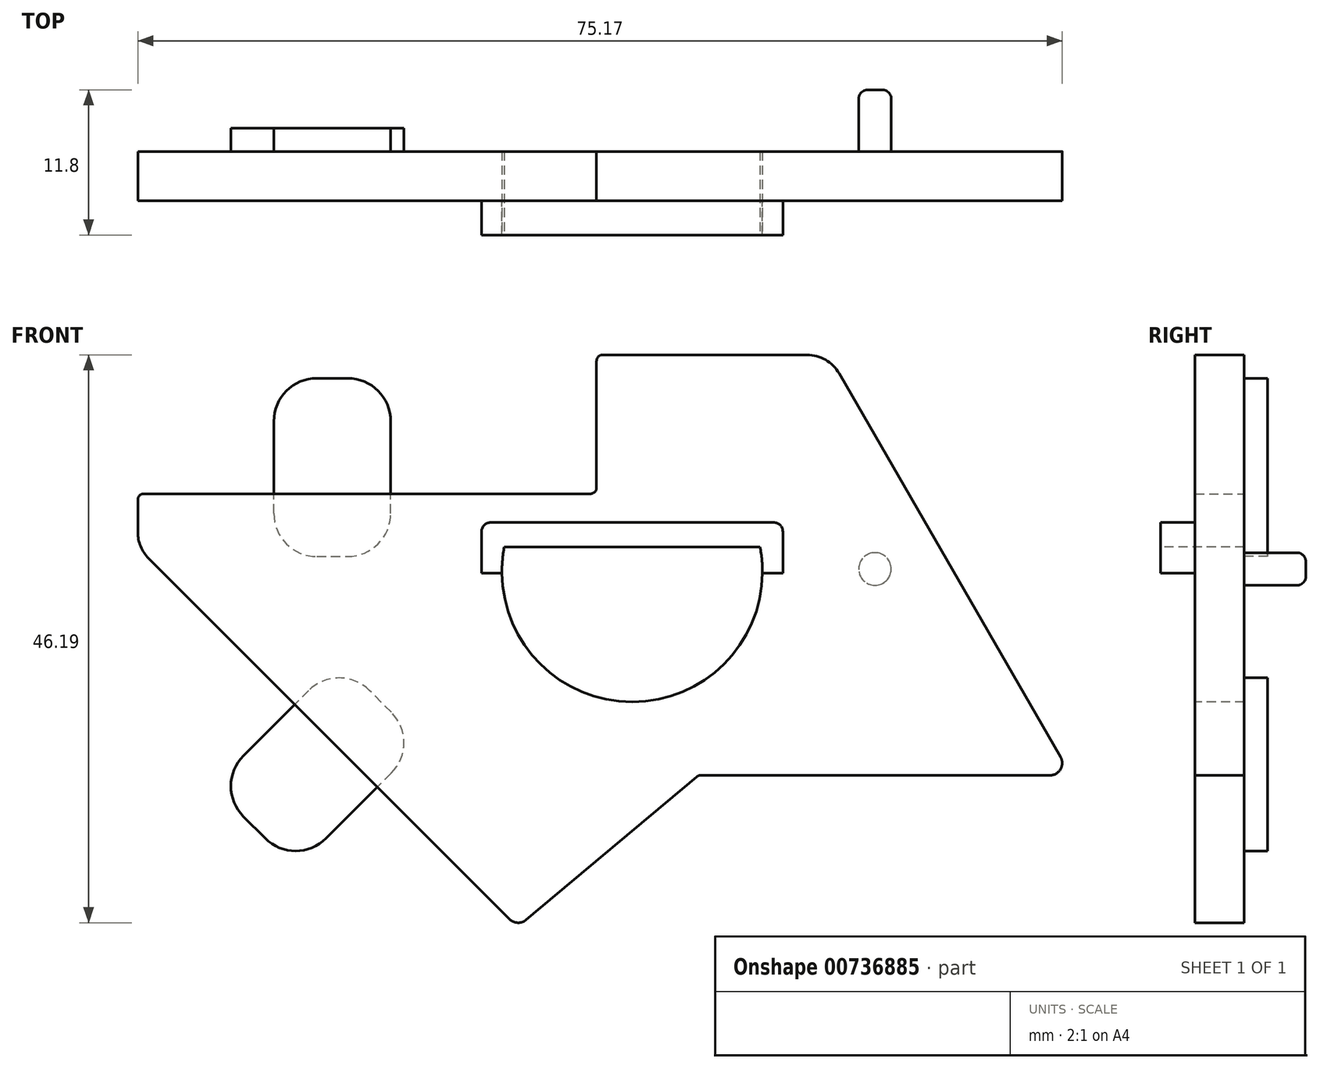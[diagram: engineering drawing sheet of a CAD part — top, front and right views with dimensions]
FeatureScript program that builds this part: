
annotation { "Feature Type Name" : "Feature", "Feature Type Description" : "" }
export const myFeature = defineFeature(function(context is Context, id is Id, definition is map)
    precondition{}
    {
        {
            var Q0;
            Q0=qCreatedBy(makeId("Front.planeOp"),FACE);
            var sketch = newSketch(context, id + "F0", { "sketchPlane" : qUnion([Q0])});
            skLineSegment(sketch, "E0", {"start": v(0, 0) * mm, "end": v(0, 11.3) * mm});
            skLineSegment(sketch, "E1", {"start": v(0, 11.3) * mm, "end": v(18.85, 11.3) * mm});
            skLineSegment(sketch, "E2", {"start": v(18.85, 11.3) * mm, "end": v(38.6, -22.9) * mm});
            skLineSegment(sketch, "E3", {"start": v(38.6, -22.9) * mm, "end": v(8.3, -22.9) * mm});
            skLineSegment(sketch, "E4", {"start": v(8.3, -22.9) * mm, "end": v(-6.42, -35.25) * mm});
            skLineSegment(sketch, "E5", {"start": v(-37.3, 0) * mm, "end": v(0, 0) * mm});
            skLineSegment(sketch, "E6", {"start": v(-37.3, 0) * mm, "end": v(-37.3, -4.37) * mm});
            skLineSegment(sketch, "E7", {"start": v(-37.3, -4.37) * mm, "end": v(-6.42, -35.25) * mm});
            skSolve(sketch);
        }
        {
            var Q0;
            Q0=makeQuery(id+"F0.imprint","IMPRINT",FACE,{"disambiguationData":[TD([[makeQuery(id+"F0.imprint","IMPRINT",EDGE,{"derivedFrom":sQuery(id+"F0.wireOp",EDGE,"E0")}),-1.0]])]});
            extrude(context, id + "F1", {"entities" : qUnion([Q0]), "depth" : 4 * mm, "offsetDistance" : 25 * mm});
        }
        {
            var Q0;
            Q0=makeQuery(id+"F1.opExtrude","SWEPT_EDGE",EDGE,{"disambiguationData":[OSD([sQuery(id+"F0.wireOp",EDGE,"E6"),sQuery(id+"F0.wireOp",EDGE,"E7")])]});
            var Q1;
            Q1=makeQuery(id+"F1.opExtrude","SWEPT_EDGE",EDGE,{"disambiguationData":[OSD([sQuery(id+"F0.wireOp",EDGE,"E1"),sQuery(id+"F0.wireOp",EDGE,"E2")])]});
            fillet(context, id + "F2", {"entities" : qUnion([Q0, Q1]), "radius" : 3 * mm, "tangentPropagation" : true, "allowEdgeOverflow" : false});
        }
        {
            var Q0;
            Q0=makeQuery(id+"F1.opExtrude","SWEPT_EDGE",EDGE,{"disambiguationData":[OSD([sQuery(id+"F0.wireOp",EDGE,"E2"),sQuery(id+"F0.wireOp",EDGE,"E3")])]});
            var Q1;
            Q1=makeQuery(id+"F1.opExtrude","SWEPT_EDGE",EDGE,{"disambiguationData":[OSD([sQuery(id+"F0.wireOp",EDGE,"E4"),sQuery(id+"F0.wireOp",EDGE,"E7")])]});
            fillet(context, id + "F3", {"entities" : qUnion([Q0, Q1]), "radius" : 1 * mm, "tangentPropagation" : true, "allowEdgeOverflow" : false});
        }
        {
            var Q0;
            Q0=makeQuery(id+"F1.opExtrude","SWEPT_EDGE",EDGE,{"disambiguationData":[OSD([sQuery(id+"F0.wireOp",EDGE,"E3"),sQuery(id+"F0.wireOp",EDGE,"E4")])]});
            var Q1;
            Q1=makeQuery(id+"F1.opExtrude","SWEPT_EDGE",EDGE,{"disambiguationData":[OSD([sQuery(id+"F0.wireOp",EDGE,"E0"),sQuery(id+"F0.wireOp",EDGE,"E5")])]});
            var Q2;
            Q2=makeQuery(id+"F1.opExtrude","SWEPT_EDGE",EDGE,{"disambiguationData":[OSD([sQuery(id+"F0.wireOp",EDGE,"E0"),sQuery(id+"F0.wireOp",EDGE,"E1")])]});
            var Q3;
            Q3=makeQuery(id+"F1.opExtrude","SWEPT_EDGE",EDGE,{"disambiguationData":[OSD([sQuery(id+"F0.wireOp",EDGE,"E5"),sQuery(id+"F0.wireOp",EDGE,"E6")])]});
            fillet(context, id + "F4", {"entities" : qUnion([Q0, Q1, Q2, Q3]), "radius" : .5 * mm, "tangentPropagation" : true, "allowEdgeOverflow" : false});
        }
        {
            var Q0;
            Q0=makeQuery(id+"F1.opExtrude","CAP_FACE",FACE,{"disambiguationData":[OSD([sQuery(id+"F0.wireOp",EDGE,"E0"),sQuery(id+"F0.wireOp",EDGE,"E1"),sQuery(id+"F0.wireOp",EDGE,"E2"),sQuery(id+"F0.wireOp",EDGE,"E3"),sQuery(id+"F0.wireOp",EDGE,"E4"),sQuery(id+"F0.wireOp",EDGE,"E5"),sQuery(id+"F0.wireOp",EDGE,"E6"),sQuery(id+"F0.wireOp",EDGE,"E7")])],"isStart":false});
            var sketch = newSketch(context, id + "F5", { "sketchPlane" : qUnion([Q0])});
            skLineSegment(sketch, "E8", {"start": v(-7.5, -4.33) * mm, "end": v(13.3, -4.33) * mm});
            skArc(sketch, "E9", {"start": v(-7.5, -4.33) * mm, "mid": v(2.9, -16.93) * mm, "end": v(13.3, -4.33) * mm});
            skSolve(sketch);
        }
        {
            var Q0;
            Q0=makeQuery(id+"F5.imprint","IMPRINT",FACE,{"disambiguationData":[TD([[makeQuery(id+"F5.imprint","IMPRINT",EDGE,{"derivedFrom":sQuery(id+"F5.wireOp",EDGE,"E8")}),-1.0]])]});
            extrude(context, id + "F6", {"entities" : qUnion([Q0]), "operationType" : NewBodyOperationType.REMOVE, "oppositeDirection" : true, "depth" : 25 * mm, "offsetDistance" : 25 * mm});
        }
        {
            var Q0;
            Q0=makeQuery(id+"F1.opExtrude","CAP_FACE",FACE,{"disambiguationData":[OSD([sQuery(id+"F0.wireOp",EDGE,"E0"),sQuery(id+"F0.wireOp",EDGE,"E1"),sQuery(id+"F0.wireOp",EDGE,"E2"),sQuery(id+"F0.wireOp",EDGE,"E3"),sQuery(id+"F0.wireOp",EDGE,"E4"),sQuery(id+"F0.wireOp",EDGE,"E5"),sQuery(id+"F0.wireOp",EDGE,"E6"),sQuery(id+"F0.wireOp",EDGE,"E7")])],"isStart":false});
            var sketch = newSketch(context, id + "F7", { "sketchPlane" : qUnion([Q0])});
            skLineSegment(sketch, "E10", {"start": v(-9.35, -2.33) * mm, "end": v(15.15, -2.33) * mm});
            skLineSegment(sketch, "E11", {"start": v(15.15, -2.33) * mm, "end": v(15.15, -6.44) * mm});
            skLineSegment(sketch, "E12", {"start": v(13.3, -4.33) * mm, "end": v(-7.5, -4.33) * mm});
            skLineSegment(sketch, "E13", {"start": v(-7.5, -4.33) * mm, "end": v(-7.7, -6.44) * mm});
            skLineSegment(sketch, "E14", {"start": v(-7.7, -6.44) * mm, "end": v(-9.35, -6.44) * mm});
            skLineSegment(sketch, "E15", {"start": v(-9.35, -6.44) * mm, "end": v(-9.35, -2.33) * mm});
            skLineSegment(sketch, "E16", {"start": v(13.3, -4.33) * mm, "end": v(13.5, -6.44) * mm});
            skLineSegment(sketch, "E17", {"start": v(13.5, -6.44) * mm, "end": v(15.15, -6.44) * mm});
            skPoint(sketch, "E18", {"position": v(2.9, -4.33) * mm});
            skPoint(sketch, "E19", {"position": v(2.9, -2.33) * mm});
            skSolve(sketch);
        }
        {
            var Q0;
            Q0=makeQuery(id+"F7.imprint","IMPRINT",FACE,{"disambiguationData":[TD([[makeQuery(id+"F7.imprint","IMPRINT",EDGE,{"derivedFrom":sQuery(id+"F7.wireOp",EDGE,"E10")}),-1.0]])]});
            extrude(context, id + "F8", {"entities" : qUnion([Q0]), "operationType" : NewBodyOperationType.ADD, "depth" : 2.8 * mm, "offsetDistance" : 25 * mm});
        }
        {
            var Q0;
            Q0=makeQuery(id+"F8.opExtrude","SWEPT_EDGE",EDGE,{"disambiguationData":[OSD([sQuery(id+"F7.wireOp",EDGE,"E10"),sQuery(id+"F7.wireOp",EDGE,"E15")])]});
            var Q1;
            Q1=makeQuery(id+"F8.opExtrude","SWEPT_EDGE",EDGE,{"disambiguationData":[OSD([sQuery(id+"F7.wireOp",EDGE,"E10"),sQuery(id+"F7.wireOp",EDGE,"E11")])]});
            fillet(context, id + "F9", {"entities" : qUnion([Q0, Q1]), "radius" : .75 * mm, "tangentPropagation" : true, "allowEdgeOverflow" : false});
        }
        {
            var Q0;
            Q0=makeQuery(id+"F1.opExtrude","CAP_FACE",FACE,{"disambiguationData":[OSD([sQuery(id+"F0.wireOp",EDGE,"E0"),sQuery(id+"F0.wireOp",EDGE,"E1"),sQuery(id+"F0.wireOp",EDGE,"E2"),sQuery(id+"F0.wireOp",EDGE,"E3"),sQuery(id+"F0.wireOp",EDGE,"E4"),sQuery(id+"F0.wireOp",EDGE,"E5"),sQuery(id+"F0.wireOp",EDGE,"E6"),sQuery(id+"F0.wireOp",EDGE,"E7")])],"isStart":true});
            var sketch = newSketch(context, id + "F10", { "sketchPlane" : qUnion([Q0])});
            skLineSegment(sketch, "E20.bottom", {"start": v(26.24, -5.1) * mm, "end": v(16.74, -5.1) * mm});
            skLineSegment(sketch, "E20.top", {"start": v(26.24, 9.4) * mm, "end": v(16.74, 9.4) * mm});
            skLineSegment(sketch, "E20.left", {"start": v(26.24, -5.1) * mm, "end": v(26.24, 9.4) * mm});
            skLineSegment(sketch, "E20.right", {"start": v(16.74, -5.1) * mm, "end": v(16.74, 9.4) * mm});
            skLineSegment(sketch, "E21.bottom", {"start": v(14.21, -20.25) * mm, "end": v(20.93, -13.53) * mm});
            skLineSegment(sketch, "E21.top", {"start": v(24.47, -30.5) * mm, "end": v(31.18, -23.78) * mm});
            skLineSegment(sketch, "E21.left", {"start": v(14.21, -20.25) * mm, "end": v(24.47, -30.5) * mm});
            skLineSegment(sketch, "E21.right", {"start": v(20.93, -13.53) * mm, "end": v(31.18, -23.78) * mm});
            skSolve(sketch);
        }
        {
            var Q0;
            {var subQ0=sQuery(id+"F10.wireOp",EDGE,"E20.top");Q0=makeQuery(id+"F10.imprint","IMPRINT",FACE,{"disambiguationData":[TD([[makeQuery(id+"F10.imprint","IMPRINT",EDGE,{"derivedFrom":subQ0}),1.0]])]});}
            var Q1;
            {var subQ0=sQuery(id+"F10.wireOp",EDGE,"E20.bottom");Q1=makeQuery(id+"F10.imprint","IMPRINT",FACE,{"disambiguationData":[TD([[makeQuery(id+"F10.imprint","IMPRINT",EDGE,{"derivedFrom":subQ0}),-1.0]])]});}
            var Q2;
            {var subQ0=sQuery(id+"F10.wireOp",EDGE,"E21.bottom");Q2=makeQuery(id+"F10.imprint","IMPRINT",FACE,{"disambiguationData":[TD([[makeQuery(id+"F10.imprint","IMPRINT",EDGE,{"derivedFrom":subQ0}),-1.0]])]});}
            var Q3;
            {var subQ0=sQuery(id+"F10.wireOp",EDGE,"E21.top");Q3=makeQuery(id+"F10.imprint","IMPRINT",FACE,{"disambiguationData":[TD([[makeQuery(id+"F10.imprint","IMPRINT",EDGE,{"derivedFrom":subQ0}),1.0]])]});}
            extrude(context, id + "F11", {"entities" : qUnion([Q0, Q1, Q2, Q3]), "operationType" : NewBodyOperationType.ADD, "depth" : 1.9 * mm, "offsetDistance" : 25 * mm});
        }
        {
            var Q0;
            Q0=makeQuery(id+"F11.opExtrude","SWEPT_EDGE",EDGE,{"disambiguationData":[OSD([sQuery(id+"F10.wireOp",EDGE,"E21.top"),sQuery(id+"F10.wireOp",EDGE,"E21.left")])]});
            var Q1;
            Q1=makeQuery(id+"F11.opExtrude","SWEPT_EDGE",EDGE,{"disambiguationData":[OSD([sQuery(id+"F10.wireOp",EDGE,"E21.top"),sQuery(id+"F10.wireOp",EDGE,"E21.right")])]});
            var Q2;
            Q2=makeQuery(id+"F11.opExtrude","SWEPT_EDGE",EDGE,{"disambiguationData":[OSD([sQuery(id+"F10.wireOp",EDGE,"E21.bottom"),sQuery(id+"F10.wireOp",EDGE,"E21.left")])]});
            var Q3;
            Q3=makeQuery(id+"F11.opExtrude","SWEPT_EDGE",EDGE,{"disambiguationData":[OSD([sQuery(id+"F10.wireOp",EDGE,"E21.bottom"),sQuery(id+"F10.wireOp",EDGE,"E21.right")])]});
            var Q4;
            Q4=makeQuery(id+"F11.opExtrude","SWEPT_EDGE",EDGE,{"disambiguationData":[OSD([sQuery(id+"F10.wireOp",EDGE,"E20.top"),sQuery(id+"F10.wireOp",EDGE,"E20.left")])]});
            var Q5;
            Q5=makeQuery(id+"F11.opExtrude","SWEPT_EDGE",EDGE,{"disambiguationData":[OSD([sQuery(id+"F10.wireOp",EDGE,"E20.top"),sQuery(id+"F10.wireOp",EDGE,"E20.right")])]});
            var Q6;
            Q6=makeQuery(id+"F11.opExtrude","SWEPT_EDGE",EDGE,{"disambiguationData":[OSD([sQuery(id+"F10.wireOp",EDGE,"E20.bottom"),sQuery(id+"F10.wireOp",EDGE,"E20.left")])]});
            var Q7;
            Q7=makeQuery(id+"F11.opExtrude","SWEPT_EDGE",EDGE,{"disambiguationData":[OSD([sQuery(id+"F10.wireOp",EDGE,"E20.bottom"),sQuery(id+"F10.wireOp",EDGE,"E20.right")])]});
            fillet(context, id + "F12", {"entities" : qUnion([Q0, Q1, Q2, Q3, Q4, Q5, Q6, Q7]), "radius" : 3.5 * mm, "tangentPropagation" : true, "allowEdgeOverflow" : false});
        }
        {
            var Q0;
            Q0=makeQuery(id+"F1.opExtrude","CAP_FACE",FACE,{"disambiguationData":[OSD([sQuery(id+"F0.wireOp",EDGE,"E0"),sQuery(id+"F0.wireOp",EDGE,"E1"),sQuery(id+"F0.wireOp",EDGE,"E2"),sQuery(id+"F0.wireOp",EDGE,"E3"),sQuery(id+"F0.wireOp",EDGE,"E4"),sQuery(id+"F0.wireOp",EDGE,"E5"),sQuery(id+"F0.wireOp",EDGE,"E6"),sQuery(id+"F0.wireOp",EDGE,"E7")])],"isStart":true});
            var sketch = newSketch(context, id + "F13", { "sketchPlane" : qUnion([Q0])});
            skCircle(sketch, "E22", {"center": v(-22.64, -6.11) * mm, "radius": 1.32 * mm});
            skPoint(sketch, "E23", {"position": v(-22.64, -4.79) * mm});
            skSolve(sketch);
        }
        {
            var Q0;
            Q0=makeQuery(id+"F13.imprint","IMPRINT",FACE,{"disambiguationData":[TD([[makeQuery(id+"F13.imprint","IMPRINT",EDGE,{"derivedFrom":sQuery(id+"F13.wireOp",EDGE,"E22")}),1.0]])]});
            extrude(context, id + "F14", {"entities" : qUnion([Q0]), "operationType" : NewBodyOperationType.ADD, "depth" : 5 * mm, "offsetDistance" : 25 * mm});
        }
        {
            var Q0;
            Q0=makeQuery(id+"F14.opExtrude","CAP_EDGE",EDGE,{"disambiguationData":[OSD([sQuery(id+"F13.wireOp",EDGE,"E22")])],"isStart":false});
            fillet(context, id + "F15", {"entities" : qUnion([Q0]), "radius" : .7 * mm, "tangentPropagation" : true, "allowEdgeOverflow" : false});
        }
    });
